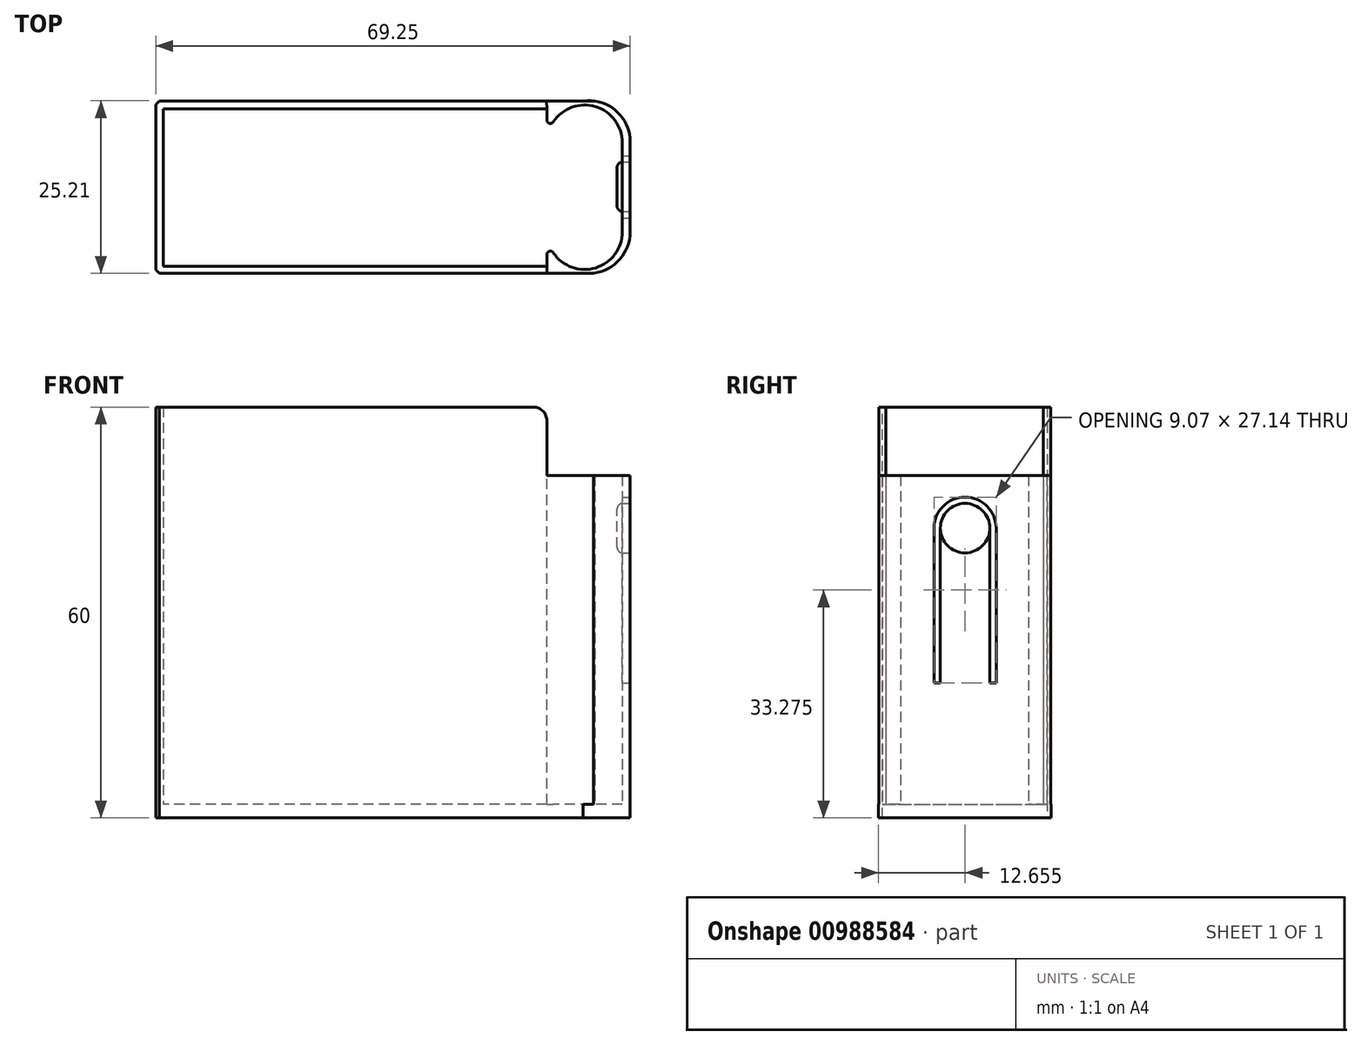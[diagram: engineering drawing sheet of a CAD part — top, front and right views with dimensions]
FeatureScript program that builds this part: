
annotation { "Feature Type Name" : "Feature", "Feature Type Description" : "" }
export const myFeature = defineFeature(function(context is Context, id is Id, definition is map)
    precondition{}
    {
        {
            var Q0;
            Q0=qCreatedBy(makeId("Top.planeOp"),FACE);
            var sketch = newSketch(context, id + "F0", { "sketchPlane" : qUnion([Q0])});
            skLineSegment(sketch, "E0.bottom", {"start": v(-46.8, 13.85) * mm, "end": v(9.2, 13.85) * mm});
            skLineSegment(sketch, "E0.top", {"start": v(-46.8, -9.15) * mm, "end": v(9.2, -9.15) * mm});
            skLineSegment(sketch, "E0.left", {"start": v(-46.8, 13.85) * mm, "end": v(-46.8, -9.15) * mm});
            skLineSegment(sketch, "E0.right", {"start": v(9.2, 13.85) * mm, "end": v(9.2, -9.15) * mm});
            skLineSegment(sketch, "E1.bottom", {"start": v(-47.9, 14.94) * mm, "end": v(17.08, 14.94) * mm});
            skLineSegment(sketch, "E1.top", {"start": v(-47.9, -10.16) * mm, "end": v(17.08, -10.16) * mm});
            skLineSegment(sketch, "E1.left", {"start": v(-47.9, 14.94) * mm, "end": v(-47.9, -10.16) * mm});
            skLineSegment(sketch, "E2.bottom", {"start": v(9.2, 8.87) * mm, "end": v(20.2, 8.87) * mm});
            skLineSegment(sketch, "E2.top", {"start": v(9.2, -4.13) * mm, "end": v(20.2, -4.13) * mm});
            skLineSegment(sketch, "E2.left", {"start": v(9.2, 8.87) * mm, "end": v(9.2, -4.13) * mm});
            skLineSegment(sketch, "E2.right", {"start": v(20.2, 8.87) * mm, "end": v(20.2, -4.13) * mm});
            skArc(sketch, "E3", {"start": v(20.2, 8.87) * mm, "mid": v(14.7, 14.37) * mm, "end": v(9.2, 8.87) * mm});
            skArc(sketch, "E4", {"start": v(9.2, -4.13) * mm, "mid": v(14.7, -9.63) * mm, "end": v(20.2, -4.13) * mm});
            skLineSegment(sketch, "E5", {"start": v(21.35, 9.02) * mm, "end": v(21.35, -4.13) * mm});
            skArc(sketch, "E6", {"start": v(21.35, 9.02) * mm, "mid": v(19.28, 13.54) * mm, "end": v(14.5, 14.94) * mm});
            skArc(sketch, "E7", {"start": v(14.5, -10.16) * mm, "mid": v(19.29, -8.69) * mm, "end": v(21.35, -4.13) * mm});
            skSolve(sketch);
        }
        {
            var Q0;
            Q0 = qSketchRegion(id + "F0", true);
            var Q1;
            {var subQ1=sQuery(id+"F0.wireOp",EDGE,"E0.bottom");Q1=makeQuery(id+"F0.imprint","IMPRINT",FACE,{"disambiguationData":[TD([[makeQuery(id+"F0.imprint","IMPRINT",EDGE,{"derivedFrom":subQ1}),-1.0]])]});}
            var Q2;
            Q2=makeQuery(id+"F0.imprint","IMPRINT",FACE,{"disambiguationData":[TD([[makeQuery(id+"F0.imprint","IMPRINT",EDGE,{"derivedFrom":sQuery(id+"F0.wireOp",EDGE,"E2.bottom")}),1.0]])]});
            var Q3;
            Q3=makeQuery(id+"F0.imprint","IMPRINT",FACE,{"disambiguationData":[TD([[makeQuery(id+"F0.imprint","IMPRINT",EDGE,{"derivedFrom":sQuery(id+"F0.wireOp",EDGE,"E2.bottom")}),-1.0]])]});
            var Q4;
            Q4=makeQuery(id+"F0.imprint","IMPRINT",FACE,{"disambiguationData":[TD([[makeQuery(id+"F0.imprint","IMPRINT",EDGE,{"derivedFrom":sQuery(id+"F0.wireOp",EDGE,"E2.top")}),-1.0]])]});
            extrude(context, id + "F1", {"entities" : qUnion([Q0, Q1, Q2, Q3, Q4]), "depth" : 2 * mm, "offsetDistance" : 25 * mm});
        }
        {
            var Q0;
            {var subQ13=sQuery(id+"F0.wireOp",EDGE,"E0.bottom");Q0=makeQuery(id+"F0.imprint","IMPRINT",FACE,{"disambiguationData":[TD([[makeQuery(id+"F0.imprint","IMPRINT",EDGE,{"derivedFrom":subQ13}),1.0]])]});}
            extrude(context, id + "F2", {"entities" : qUnion([Q0]), "operationType" : NewBodyOperationType.ADD, "depth" : 50 * mm, "offsetDistance" : 25 * mm});
        }
        {
            var Q0;
            Q0=makeQuery(id+"F2.opExtrude","SWEPT_EDGE",EDGE,{"disambiguationData":[OSD([sQuery(id+"F0.wireOp",EDGE,"E0.right"),sQuery(id+"F0.wireOp",EDGE,"E2.bottom"),sQuery(id+"F0.wireOp",EDGE,"E2.left"),sQuery(id+"F0.wireOp",EDGE,"E3")])]});
            var Q1;
            Q1=makeQuery(id+"F2.opExtrude","SWEPT_EDGE",EDGE,{"disambiguationData":[OSD([sQuery(id+"F0.wireOp",EDGE,"E0.right"),sQuery(id+"F0.wireOp",EDGE,"E2.top"),sQuery(id+"F0.wireOp",EDGE,"E2.left"),sQuery(id+"F0.wireOp",EDGE,"E4")])]});
            fillet(context, id + "F3", {"entities" : qUnion([Q0, Q1]), "radius" : 0.5 * mm, "tangentPropagation" : true, "allowEdgeOverflow" : false});
        }
        {
            var Q0;
            {var subQ0=sQuery(id+"F0.wireOp",EDGE,"E1.left");var subQ1=sQuery(id+"F0.wireOp",EDGE,"E1.bottom");Q0=makeQuery(id+"F2.boolean.opBoolean","MERGE",EDGE,{"derivedFrom":[makeQuery(id+"F1.opExtrude","SWEPT_EDGE",EDGE,{"disambiguationData":[OSD([subQ1,subQ0])]}),makeQuery(id+"F2.opExtrude","SWEPT_EDGE",EDGE,{"disambiguationData":[OSD([subQ1,subQ0])]})]});}
            var Q1;
            {var subQ0=sQuery(id+"F0.wireOp",EDGE,"E1.left");var subQ1=sQuery(id+"F0.wireOp",EDGE,"E1.top");Q1=makeQuery(id+"F2.boolean.opBoolean","MERGE",EDGE,{"derivedFrom":[makeQuery(id+"F1.opExtrude","SWEPT_EDGE",EDGE,{"disambiguationData":[OSD([subQ1,subQ0])]}),makeQuery(id+"F2.opExtrude","SWEPT_EDGE",EDGE,{"disambiguationData":[OSD([subQ1,subQ0])]})]});}
            chamfer(context, id + "F4", {"entities" : qUnion([Q0, Q1]), "width" : 0.5 * mm, "tangentPropagation" : true});
        }
        {
            var Q0;
            Q0=makeQuery(id+"F2.opExtrude","CAP_FACE",FACE,{"disambiguationData":[OSD([sQuery(id+"F0.wireOp",EDGE,"E0.bottom"),sQuery(id+"F0.wireOp",EDGE,"E0.top"),sQuery(id+"F0.wireOp",EDGE,"E0.left"),sQuery(id+"F0.wireOp",EDGE,"E0.right"),sQuery(id+"F0.wireOp",EDGE,"E1.bottom"),sQuery(id+"F0.wireOp",EDGE,"E1.top"),sQuery(id+"F0.wireOp",EDGE,"E1.left"),sQuery(id+"F0.wireOp",EDGE,"E2.right"),sQuery(id+"F0.wireOp",EDGE,"E3"),sQuery(id+"F0.wireOp",EDGE,"E4"),sQuery(id+"F0.wireOp",EDGE,"E5"),sQuery(id+"F0.wireOp",EDGE,"E6"),sQuery(id+"F0.wireOp",EDGE,"E7")])],"isStart":false});
            var sketch = newSketch(context, id + "F5", { "sketchPlane" : qUnion([Q0])});
            skLineSegment(sketch, "E8", {"start": v(9.2, 13.85) * mm, "end": v(9.16, 14.94) * mm});
            skLineSegment(sketch, "E9", {"start": v(9.2, -9.15) * mm, "end": v(9.2, -10.16) * mm});
            skSolve(sketch);
        }
        {
            var Q0;
            {var subQ3=sQuery(id+"F5.wireOp",EDGE,"E8");Q0=makeQuery(id+"F5.imprint","IMPRINT",FACE,{"disambiguationData":[TD([[makeQuery(id+"F5.imprint","IMPRINT",EDGE,{"derivedFrom":subQ3}),1.0]])]});}
            extrude(context, id + "F6", {"entities" : qUnion([Q0]), "operationType" : NewBodyOperationType.ADD, "depth" : 10 * mm, "offsetDistance" : 25 * mm});
        }
        {
            var Q0;
            Q0=makeQuery(id+"F6.opExtrude","CAP_EDGE",EDGE,{"disambiguationData":[OSD([sQuery(id+"F5.wireOp",EDGE,"E9")])],"isStart":false});
            var Q1;
            Q1=makeQuery(id+"F6.opExtrude","CAP_EDGE",EDGE,{"disambiguationData":[OSD([sQuery(id+"F5.wireOp",EDGE,"E8")])],"isStart":false});
            fillet(context, id + "F7", {"entities" : qUnion([Q0, Q1]), "radius" : 2 * mm, "tangentPropagation" : true, "allowEdgeOverflow" : false});
        }
        {
            var Q0;
            {var subQ0=sQuery(id+"F0.wireOp",EDGE,"E5");Q0=makeQuery(id+"F2.boolean.opBoolean","MERGE",FACE,{"derivedFrom":[makeQuery(id+"F1.opExtrude","SWEPT_FACE",FACE,{"disambiguationData":[OSD([subQ0])]}),makeQuery(id+"F2.opExtrude","SWEPT_FACE",FACE,{"disambiguationData":[OSD([subQ0])]})]});}
            var sketch = newSketch(context, id + "F8", { "sketchPlane" : qUnion([Q0])});
            skLineSegment(sketch, "E10", {"start": v(2.44, 47.94) * mm, "end": v(2.44, 18.65) * mm});
            skLineSegment(sketch, "E11", {"start": v(6.06, 19.7) * mm, "end": v(6.06, 42.31) * mm});
            skLineSegment(sketch, "E12", {"start": v(6.98, 42.31) * mm, "end": v(6.98, 19.7) * mm});
            skLineSegment(sketch, "E13", {"start": v(6.98, 19.7) * mm, "end": v(6.06, 19.7) * mm});
            skLineSegment(sketch, "E14.MirrorCS", {"start": v(-1.17, 19.7) * mm, "end": v(-1.17, 42.31) * mm});
            skLineSegment(sketch, "E15.MirrorCS", {"start": v(-2.09, 19.7) * mm, "end": v(-1.17, 19.7) * mm});
            skLineSegment(sketch, "E16.MirrorCS", {"start": v(-2.09, 42.31) * mm, "end": v(-2.09, 19.7) * mm});
            skArc(sketch, "E17", {"start": v(6.06, 42.31) * mm, "mid": v(2.44, 45.92) * mm, "end": v(-1.17, 42.31) * mm});
            skArc(sketch, "E18", {"start": v(6.98, 42.31) * mm, "mid": v(2.44, 46.85) * mm, "end": v(-2.09, 42.31) * mm});
            skSolve(sketch);
        }
        {
            var Q0;
            {var subQ1=sQuery(id+"F8.wireOp",EDGE,"E14.MirrorCS");Q0=makeQuery(id+"F8.imprint","IMPRINT",FACE,{"disambiguationData":[TD([[makeQuery(id+"F8.imprint","IMPRINT",EDGE,{"derivedFrom":subQ1}),1.0]])]});}
            var Q1;
            {var subQ1=sQuery(id+"F8.wireOp",EDGE,"E11");Q1=makeQuery(id+"F8.imprint","IMPRINT",FACE,{"disambiguationData":[TD([[makeQuery(id+"F8.imprint","IMPRINT",EDGE,{"derivedFrom":subQ1}),-1.0]])]});}
            extrude(context, id + "F9", {"entities" : qUnion([Q0, Q1]), "operationType" : NewBodyOperationType.REMOVE, "oppositeDirection" : true, "depth" : 25 * mm, "offsetDistance" : 25 * mm});
        }
        {
            var Q0;
            {var subQ0=sQuery(id+"F0.wireOp",EDGE,"E5");Q0=makeQuery(id+"F2.boolean.opBoolean","MERGE",FACE,{"derivedFrom":[makeQuery(id+"F1.opExtrude","SWEPT_FACE",FACE,{"disambiguationData":[OSD([subQ0])]}),makeQuery(id+"F2.opExtrude","SWEPT_FACE",FACE,{"disambiguationData":[OSD([subQ0])]})]});}
            var sketch = newSketch(context, id + "F10", { "sketchPlane" : qUnion([Q0])});
            skCircle(sketch, "E19", {"center": v(2.44, 42.31) * mm, "radius": 3.61 * mm});
            skSolve(sketch);
        }
        {
            var Q0;
            {var subQ0=sQuery(id+"F10.wireOp",EDGE,"E19");var subQ1=makeQuery(id+"F10.imprint","INTERSECT",VERTEX,{"derivedFrom":[makeQuery(id+"F9.boolean.opBoolean","COPY",EDGE,{"derivedFrom":makeQuery(id+"F9.opExtrude","CAP_EDGE",EDGE,{"disambiguationData":[OSD([sQuery(id+"F8.wireOp",EDGE,"E11")])],"isStart":true})}),subQ0]});Q0=makeQuery(id+"F10.imprint","IMPRINT",FACE,{"disambiguationData":[TD([[makeQuery(id+"F10.imprint","IMPRINT",EDGE,{"disambiguationData":[TD([[subQ1,-1.0]])],"derivedFrom":subQ0}),1.0]])]});}
            extrude(context, id + "F11", {"entities" : qUnion([Q0]), "oppositeDirection" : true, "depth" : 1.9 * mm, "offsetDistance" : 25 * mm});
        }
        {
            var Q0;
            Q0=makeQuery(id+"F11.opExtrude","CAP_FACE",FACE,{"disambiguationData":[OSD([sQuery(id+"F10.wireOp",EDGE,"E19")])],"isStart":false});
            fillet(context, id + "F12", {"entities" : qUnion([Q0]), "radius" : 0.8 * mm, "tangentPropagation" : true, "allowEdgeOverflow" : false});
        }
    });
